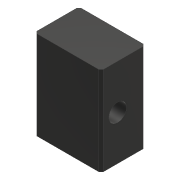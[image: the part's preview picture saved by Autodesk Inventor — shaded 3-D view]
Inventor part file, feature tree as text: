
AUTODESK INVENTOR PART (.ipt)
format: ipt  version: 2018 (Build 220112000, 112)  size: 90,624 bytes
history: native  units: mm
features: extrude x1, chamfer x1, sketch x1
ambient origin geometry x8: Origin, YZ Plane, XZ Plane, XY Plane, X Axis, Y Axis, Z Axis, Center Point
bodies: Solid1 (feature_tree)
feature tree (3):
  extrude  "Extrusion1"  Depth=40.0mm
  chamfer  "Chamfer1"  Distance=15.0mm
  sketch  "Sketch1"  dims[d0=80.0mm d1=40.0mm d2=15.0mm d3=16.0mm d4=60.0mm d5=0.0mm d6=2.0mm d7=2.0mm d8=45.0deg]
